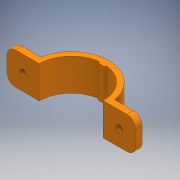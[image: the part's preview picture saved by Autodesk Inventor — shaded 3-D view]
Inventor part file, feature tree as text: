
AUTODESK INVENTOR PART (.ipt)
format: ipt  version: 2018 (Build 220112000, 112)  size: 139,264 bytes
history: native  units: mm
features: sketch x2, extrude x1, hole x1, mirror x1, fillet x1
ambient origin geometry x8: Origin, YZ Plane, XZ Plane, XY Plane, X Axis, Y Axis, Z Axis, Center Point
bodies: Solid1 (feature_tree)
feature tree (6):
  extrude  "Extrusion1"  Depth=14.865mm
  hole  "Hole1"  [1 undecoded]
  mirror  "Mirror1"
  fillet  "Fillet1"  Radius=15.0mm
  sketch  "Sketch1"  dims[d0=3.0mm d1=14.865mm]
  sketch  "Sketch2"  dims[d3=2.5mm d6=15.0mm d7=0.0mm d8=15.0mm d9=3.0mm d10=6.0mm d11=4.0mm d12=2.0mm d13=90.0deg d14=8.0mm d15=20.594885mm d16=4.0mm d17=0.9mm d18=3.0mm]
note: 1 required parameter value undecoded (feature->parameter linkage not recoverable at this tier; creation-order binding heuristic only, values carry confidence <= 0.55)
